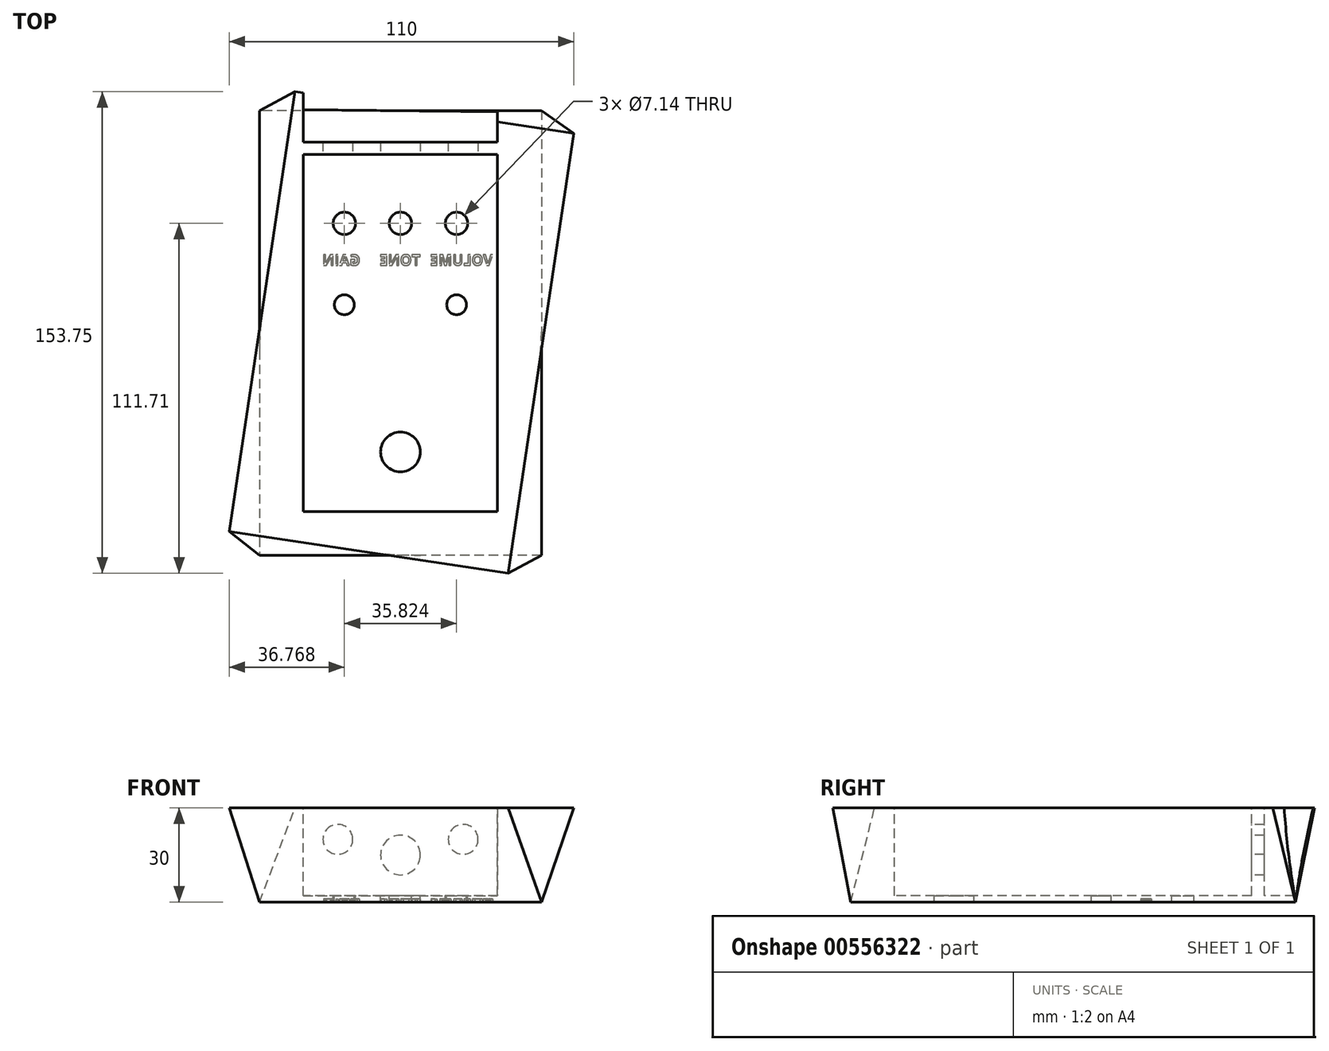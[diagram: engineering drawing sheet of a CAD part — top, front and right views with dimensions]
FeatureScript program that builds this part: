
annotation { "Feature Type Name" : "Feature", "Feature Type Description" : "" }
export const myFeature = defineFeature(function(context is Context, id is Id, definition is map)
    precondition{}
    {
        {
            var Q0;
            Q0=qCreatedBy(makeId("Top.planeOp"),FACE);
            var sketch = newSketch(context, id + "F0", { "sketchPlane" : qUnion([Q0])});
            skLineSegment(sketch, "E0.bottom", {"start": v(-35, 61) * mm, "end": v(35, 61) * mm});
            skLineSegment(sketch, "E0.top", {"start": v(-35, -61) * mm, "end": v(35, -61) * mm});
            skLineSegment(sketch, "E0.left", {"start": v(-35, 61) * mm, "end": v(-35, -61) * mm});
            skLineSegment(sketch, "E0.right", {"start": v(35, 61) * mm, "end": v(35, -61) * mm});
            skSolve(sketch);
        }
        {
            var Q0;
            Q0=makeQuery(id+"F0.imprint","IMPRINT",FACE,{"disambiguationData":[TD([[makeQuery(id+"F0.imprint","IMPRINT",EDGE,{"derivedFrom":sQuery(id+"F0.wireOp",EDGE,"E0.bottom")}),-1.0]])]});
            extrude(context, id + "F1", {"entities" : qUnion([Q0]), "depth" : 30 * mm, "offsetDistance" : 25 * mm});
        }
        {
            var Q0;
            {var subQ0=sQuery(id+"F0.wireOp",EDGE,"E0.bottom");var subQ1=sQuery(id+"F0.wireOp",EDGE,"E0.left");var subQ2=sQuery(id+"F0.wireOp",EDGE,"E0.top");var subQ3=sQuery(id+"F0.wireOp",EDGE,"E0.right");Q0=makeQuery(id+"F13.boolean.opBoolean","SPLIT",FACE,{"disambiguationData":[TD([makeQuery(id+"F1.opExtrude","SWEPT_FACE",FACE,{"disambiguationData":[OSD([subQ0])]})])],"derivedFrom":makeQuery(id+"F1.opExtrude","CAP_FACE",FACE,{"disambiguationData":[OSD([subQ0,subQ2,subQ1,subQ3])],"isStart":true})});}
            var sketch = newSketch(context, id + "F2", { "sketchPlane" : qUnion([Q0])});
            skLineSegment(sketch, "E1.bottom", {"start": v(45, -71) * mm, "end": v(-45, -71) * mm});
            skLineSegment(sketch, "E1.top", {"start": v(45, 71) * mm, "end": v(-45, 71) * mm});
            skLineSegment(sketch, "E1.left", {"start": v(45, -71) * mm, "end": v(45, 71) * mm});
            skLineSegment(sketch, "E1.right", {"start": v(-45, -71) * mm, "end": v(-45, 71) * mm});
            skPoint(sketch, "E1.middle", {"position": v(0, 0) * mm});
            skSolve(sketch);
        }
        {
            var Q0;
            Q0=makeQuery(id+"F1.opExtrude","CAP_FACE",FACE,{"disambiguationData":[OSD([sQuery(id+"F0.wireOp",EDGE,"E0.bottom"),sQuery(id+"F0.wireOp",EDGE,"E0.top"),sQuery(id+"F0.wireOp",EDGE,"E0.left"),sQuery(id+"F0.wireOp",EDGE,"E0.right")])],"isStart":false});
            var sketch = newSketch(context, id + "F3", { "sketchPlane" : qUnion([Q0])});
            skLineSegment(sketch, "E2.bottom", {"start": v(-33.69, 77.04) * mm, "end": v(55.32, 63.73) * mm});
            skLineSegment(sketch, "E2.top", {"start": v(-54.68, -63.4) * mm, "end": v(34.34, -76.7) * mm});
            skLineSegment(sketch, "E2.left", {"start": v(-33.69, 77.04) * mm, "end": v(-54.68, -63.4) * mm});
            skLineSegment(sketch, "E2.right", {"start": v(55.32, 63.73) * mm, "end": v(34.34, -76.7) * mm});
            skPoint(sketch, "E2.middle", {"position": v(0, 0) * mm});
            skSolve(sketch);
        }
        {
            var Q0;
            Q0 = qSketchRegion(id + "F2", true);
            var Q1;
            Q1 = qSketchRegion(id + "F3", true);
            var Q2;
            Q2=sQuery(id+"F2.wireOp",VERTEX,"E1.left.start");
            var Q3;
            Q3=sQuery(id+"F3.wireOp",VERTEX,"E2.right.start");
            loft(context, id + "F4", {"operationType" : NewBodyOperationType.ADD, "sheetProfilesArray" : [{ "sheetProfileEntities" : qUnion([Q0]) }, { "sheetProfileEntities" : qUnion([Q1]) }], "matchConnections" : true, "connections" : [{ "connectionEntities" : qUnion([Q2, Q3]), "connectionEdgeQueries" : qUnion([]), "connectionEdgeParameters" : [] }]});
        }
        {
            var Q0;
            Q0=makeQuery(id+"F1.opExtrude","CAP_FACE",FACE,{"disambiguationData":[OSD([sQuery(id+"F0.wireOp",EDGE,"E0.bottom"),sQuery(id+"F0.wireOp",EDGE,"E0.top"),sQuery(id+"F0.wireOp",EDGE,"E0.left"),sQuery(id+"F0.wireOp",EDGE,"E0.right")])],"isStart":false});
            var sketch = newSketch(context, id + "F5", { "sketchPlane" : qUnion([Q0])});
            skLineSegment(sketch, "E3.bottom", {"start": v(-31, 57) * mm, "end": v(31, 57) * mm});
            skLineSegment(sketch, "E3.top", {"start": v(-31, -57) * mm, "end": v(31, -57) * mm});
            skLineSegment(sketch, "E3.left", {"start": v(-31, 57) * mm, "end": v(-31, -57) * mm});
            skLineSegment(sketch, "E3.right", {"start": v(31, 57) * mm, "end": v(31, -57) * mm});
            skSolve(sketch);
        }
        {
            var Q0;
            Q0=makeQuery(id+"F5.imprint","IMPRINT",FACE,{"disambiguationData":[TD([[makeQuery(id+"F5.imprint","IMPRINT",EDGE,{"derivedFrom":sQuery(id+"F5.wireOp",EDGE,"E3.bottom")}),-1.0]])]});
            extrude(context, id + "F6", {"entities" : qUnion([Q0]), "operationType" : NewBodyOperationType.REMOVE, "oppositeDirection" : true, "depth" : 28 * mm, "offsetDistance" : 25 * mm});
        }
        {
            var Q0;
            Q0=makeQuery(id+"F6.boolean.opBoolean","COPY",FACE,{"derivedFrom":makeQuery(id+"F6.opExtrude","CAP_FACE",FACE,{"disambiguationData":[OSD([sQuery(id+"F5.wireOp",EDGE,"E3.bottom"),sQuery(id+"F5.wireOp",EDGE,"E3.top"),sQuery(id+"F5.wireOp",EDGE,"E3.left"),sQuery(id+"F5.wireOp",EDGE,"E3.right")])],"isStart":false})});
            var sketch = newSketch(context, id + "F7", { "sketchPlane" : qUnion([Q0])});
            skCircle(sketch, "E4", {"center": v(-17.91, 35) * mm, "radius": 3.57 * mm});
            skCircle(sketch, "E5", {"center": v(0, 35) * mm, "radius": 3.57 * mm});
            skCircle(sketch, "E6", {"center": v(17.91, 35) * mm, "radius": 3.57 * mm});
            skCircle(sketch, "E7", {"center": v(17.91, 9) * mm, "radius": 3.17 * mm});
            skCircle(sketch, "E8", {"center": v(0, -38) * mm, "radius": 6.35 * mm});
            skCircle(sketch, "E9", {"center": v(-17.91, 9) * mm, "radius": 3.17 * mm});
            skSolve(sketch);
        }
        {
            var Q0;
            Q0=qSketchRegion(id+"F7",true);
            extrude(context, id + "F8", {"entities" : qUnion([Q0]), "operationType" : NewBodyOperationType.REMOVE, "oppositeDirection" : true, "depth" : 25 * mm, "offsetDistance" : 25 * mm});
        }
        {
            var Q0;
            Q0=makeQuery(id+"F6.boolean.opBoolean","COPY",FACE,{"derivedFrom":makeQuery(id+"F6.opExtrude","SWEPT_FACE",FACE,{"disambiguationData":[OSD([sQuery(id+"F5.wireOp",EDGE,"E3.bottom")])]})});
            var sketch = newSketch(context, id + "F9", { "sketchPlane" : qUnion([Q0])});
            skCircle(sketch, "E10", {"center": v(0, 15) * mm, "radius": 6.35 * mm});
            skCircle(sketch, "E11", {"center": v(20, 20) * mm, "radius": 4.76 * mm});
            skCircle(sketch, "E12", {"center": v(-20, 20) * mm, "radius": 4.76 * mm});
            skSolve(sketch);
        }
        {
            var Q0;
            Q0=qSketchRegion(id+"F9",true);
            extrude(context, id + "F10", {"entities" : qUnion([Q0]), "operationType" : NewBodyOperationType.REMOVE, "oppositeDirection" : true, "depth" : 25 * mm, "offsetDistance" : 25 * mm});
        }
        {
            var Q0;
            Q0=qCreatedBy(makeId("Front.planeOp"),FACE);
            cPlane(context, id + "F11", {"entities" : qUnion([Q0]), "cplaneType" : CPlaneType.OFFSET, "offset" : 38 * mm, "width" : 150 * mm, "height" : 150 * mm});
        }
        {
            var Q0;
            Q0=makeQuery(id+"F1.opExtrude","CAP_FACE",FACE,{"disambiguationData":[OSD([sQuery(id+"F0.wireOp",EDGE,"E0.bottom"),sQuery(id+"F0.wireOp",EDGE,"E0.top"),sQuery(id+"F0.wireOp",EDGE,"E0.left"),sQuery(id+"F0.wireOp",EDGE,"E0.right")])],"isStart":true});
            var sketch = newSketch(context, id + "F12", { "sketchPlane" : qUnion([Q0])});
            skText(sketch, "E13", { "text": "VOLUME", "fontName": "OpenSans-Bold.ttf"});
            skText(sketch, "E14", { "text": "TONE", "fontName": "OpenSans-Bold.ttf"});
            skText(sketch, "E15", { "text": "GAIN", "fontName": "OpenSans-Bold.ttf"});
            const initialGuessF12  = {"E13": [0.02947, -0.02163, -1, 0, 0.00337], "E14": [0.00634, -0.0216, -1, 0, 0.0034], "E15": [-0.01283, -0.02159, -1, 0, 0.00341]};
            skSetInitialGuess(sketch, initialGuessF12);
            skSolve(sketch);
        }
        {
            var Q0;
            Q0=qSketchRegion(id+"F12",true);
            extrude(context, id + "F13", {"entities" : qUnion([Q0]), "operationType" : NewBodyOperationType.REMOVE, "oppositeDirection" : true, "depth" : 1 * mm, "offsetDistance" : 25 * mm});
        }
        {
            var Q0;
            Q0=makeQuery(id+"F6.boolean.opBoolean","COPY",FACE,{"derivedFrom":makeQuery(id+"F6.opExtrude","SWEPT_FACE",FACE,{"disambiguationData":[OSD([sQuery(id+"F5.wireOp",EDGE,"E3.bottom")])]})});
            cPlane(context, id + "F14", {"entities" : qUnion([Q0]), "cplaneType" : CPlaneType.OFFSET, "offset" : 4 * mm, "oppositeDirection" : true, "width" : 150 * mm, "height" : 150 * mm});
        }
        {
            var Q0;
            Q0=qCreatedBy(id+"F14.planeOp",FACE);
            var sketch = newSketch(context, id + "F15", { "sketchPlane" : qUnion([Q0])});
            skLineSegment(sketch, "E16.0", {"start": v(-31, 30) * mm, "end": v(31, 30) * mm});
            skLineSegment(sketch, "E17.0", {"start": v(31, 2) * mm, "end": v(31, 30) * mm});
            skLineSegment(sketch, "E18.0.0", {"start": v(31, 30) * mm, "end": v(-31, 30) * mm});
            skLineSegment(sketch, "E18.0.1", {"start": v(-31, 30) * mm, "end": v(-31, 2) * mm});
            skLineSegment(sketch, "E18.0.2", {"start": v(-31, 2) * mm, "end": v(31, 2) * mm});
            skLineSegment(sketch, "E19.0", {"start": v(-31, 2) * mm, "end": v(-31, 30) * mm});
            skSolve(sketch);
        }
        {
            var Q0;
            Q0 = qSketchRegion(id + "F15", true);
            extrude(context, id + "F16", {"entities" : qUnion([Q0]), "operationType" : NewBodyOperationType.REMOVE, "oppositeDirection" : true, "depth" : 25 * mm, "offsetDistance" : 25 * mm});
        }
    });
